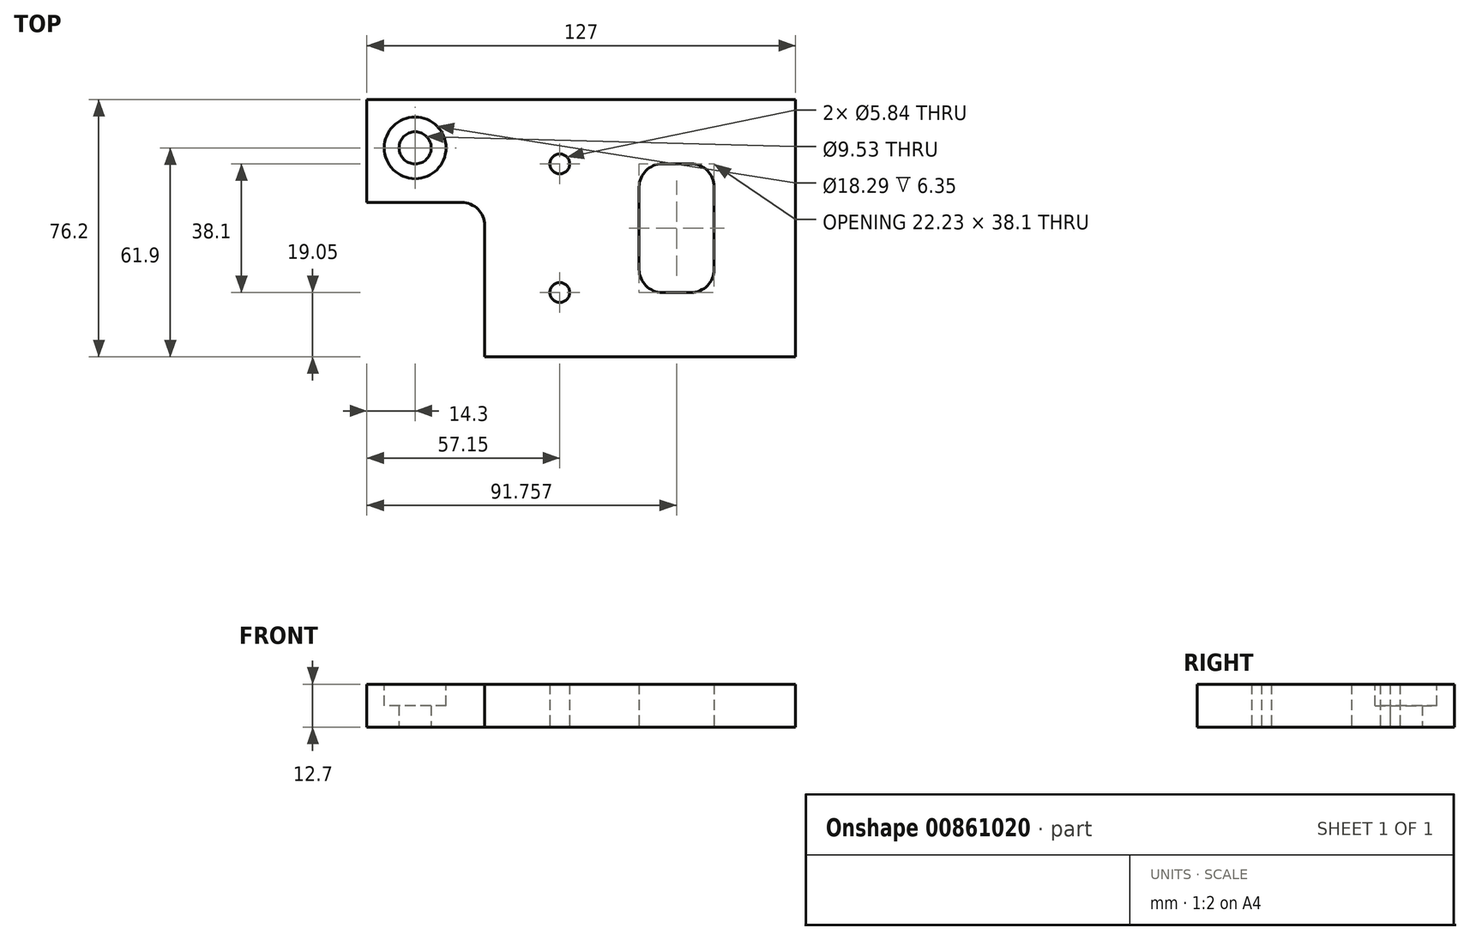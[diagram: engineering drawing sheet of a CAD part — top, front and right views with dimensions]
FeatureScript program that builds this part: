
annotation { "Feature Type Name" : "Feature", "Feature Type Description" : "" }
export const myFeature = defineFeature(function(context is Context, id is Id, definition is map)
    precondition{}
    {
        {
            var Q0;
            Q0=qCreatedBy(makeId("Top.planeOp"),FACE);
            var sketch = newSketch(context, id + "F0", { "sketchPlane" : qUnion([Q0])});
            skLineSegment(sketch, "E0.bottom", {"start": v(0, 0) * mm, "end": v(127, 0) * mm});
            skLineSegment(sketch, "E0.top", {"start": v(34.93, -76.2) * mm, "end": v(127, -76.2) * mm});
            skLineSegment(sketch, "E0.left", {"start": v(0, 0) * mm, "end": v(0, -30.48) * mm});
            skLineSegment(sketch, "E0.right", {"start": v(127, 0) * mm, "end": v(127, -76.2) * mm});
            skPoint(sketch, "E1", {"position": v(0, -30.48) * mm});
            skPoint(sketch, "E2", {"position": v(34.93, -76.2) * mm});
            skLineSegment(sketch, "E3", {"start": v(34.93, -76.2) * mm, "end": v(34.93, -37.34) * mm});
            skLineSegment(sketch, "E4", {"start": v(28.07, -30.48) * mm, "end": v(0, -30.48) * mm});
            skPoint(sketch, "E5.visualSharp", {"position": v(34.93, -30.48) * mm});
            skArc(sketch, "E5.filletArc", {"start": v(34.93, -37.34) * mm, "mid": v(32.92, -32.49) * mm, "end": v(28.07, -30.48) * mm});
            skPoint(sketch, "E6", {"position": v(91.76, -38.1) * mm});
            skLineSegment(sketch, "E7.bottom", {"start": v(96.01, -57.15) * mm, "end": v(87.5, -57.15) * mm});
            skLineSegment(sketch, "E7.top", {"start": v(96.01, -19.05) * mm, "end": v(87.5, -19.05) * mm});
            skLineSegment(sketch, "E7.left", {"start": v(102.87, -50.3) * mm, "end": v(102.87, -25.9) * mm});
            skLineSegment(sketch, "E7.right", {"start": v(80.64, -50.3) * mm, "end": v(80.64, -25.9) * mm});
            skPoint(sketch, "E8.visualSharp", {"position": v(80.64, -19.05) * mm});
            skArc(sketch, "E8.filletArc", {"start": v(87.5, -19.05) * mm, "mid": v(82.65, -21.06) * mm, "end": v(80.64, -25.9) * mm});
            skPoint(sketch, "E9.visualSharp", {"position": v(102.87, -19.05) * mm});
            skArc(sketch, "E9.filletArc", {"start": v(102.87, -25.9) * mm, "mid": v(100.86, -21.06) * mm, "end": v(96.01, -19.05) * mm});
            skPoint(sketch, "E10.visualSharp", {"position": v(102.87, -57.15) * mm});
            skArc(sketch, "E10.filletArc", {"start": v(96.01, -57.15) * mm, "mid": v(100.86, -55.14) * mm, "end": v(102.87, -50.3) * mm});
            skPoint(sketch, "E11.visualSharp", {"position": v(80.64, -57.15) * mm});
            skArc(sketch, "E11.filletArc", {"start": v(80.64, -50.3) * mm, "mid": v(82.65, -55.14) * mm, "end": v(87.5, -57.15) * mm});
            skCircle(sketch, "E12", {"center": v(57.15, -19.05) * mm, "radius": 2.92 * mm});
            skLineSegment(sketch, "E13", {"start": v(115.8, -38.1) * mm, "end": v(62.57, -38.1) * mm, "construction": true});
            skCircle(sketch, "E14.MirrorC", {"center": v(57.15, -57.15) * mm, "radius": 2.92 * mm});
            skCircle(sketch, "E15", {"center": v(14.3, -14.3) * mm, "radius": 4.76 * mm});
            skSolve(sketch);
        }
        {
            var Q0;
            Q0 = qSketchRegion(id + "F0", true);
            extrude(context, id + "F1", {"entities" : qUnion([Q0]), "depth" : 12.7 * mm, "offsetDistance" : 25.4 * mm});
        }
        {
            var Q0;
            Q0=makeQuery(id+"F1.opExtrude","CAP_FACE",FACE,{"disambiguationData":[OSD([sQuery(id+"F0.wireOp",EDGE,"E0.bottom"),sQuery(id+"F0.wireOp",EDGE,"E0.top"),sQuery(id+"F0.wireOp",EDGE,"E0.left"),sQuery(id+"F0.wireOp",EDGE,"E0.right"),sQuery(id+"F0.wireOp",EDGE,"E3"),sQuery(id+"F0.wireOp",EDGE,"E4"),sQuery(id+"F0.wireOp",EDGE,"E5.filletArc"),sQuery(id+"F0.wireOp",EDGE,"E7.bottom"),sQuery(id+"F0.wireOp",EDGE,"E7.top"),sQuery(id+"F0.wireOp",EDGE,"E7.left"),sQuery(id+"F0.wireOp",EDGE,"E7.right"),sQuery(id+"F0.wireOp",EDGE,"E8.filletArc"),sQuery(id+"F0.wireOp",EDGE,"E9.filletArc"),sQuery(id+"F0.wireOp",EDGE,"E10.filletArc"),sQuery(id+"F0.wireOp",EDGE,"E11.filletArc"),sQuery(id+"F0.wireOp",EDGE,"E12"),sQuery(id+"F0.wireOp",EDGE,"E14.MirrorC"),sQuery(id+"F0.wireOp",EDGE,"E15")])],"isStart":false});
            var sketch = newSketch(context, id + "F2", { "sketchPlane" : qUnion([Q0])});
            skCircle(sketch, "E16", {"center": v(14.3, -14.3) * mm, "radius": 9.14 * mm});
            skSolve(sketch);
        }
        {
            var Q0;
            Q0=makeQuery(id+"F2.imprint","IMPRINT",FACE,{"disambiguationData":[TD([[makeQuery(id+"F2.imprint","IMPRINT",EDGE,{"derivedFrom":sQuery(id+"F2.wireOp",EDGE,"E16")}),1.0]])]});
            extrude(context, id + "F3", {"entities" : qUnion([Q0]), "operationType" : NewBodyOperationType.REMOVE, "oppositeDirection" : true, "depth" : 6.35 * mm, "offsetDistance" : 25.4 * mm});
        }
    });
